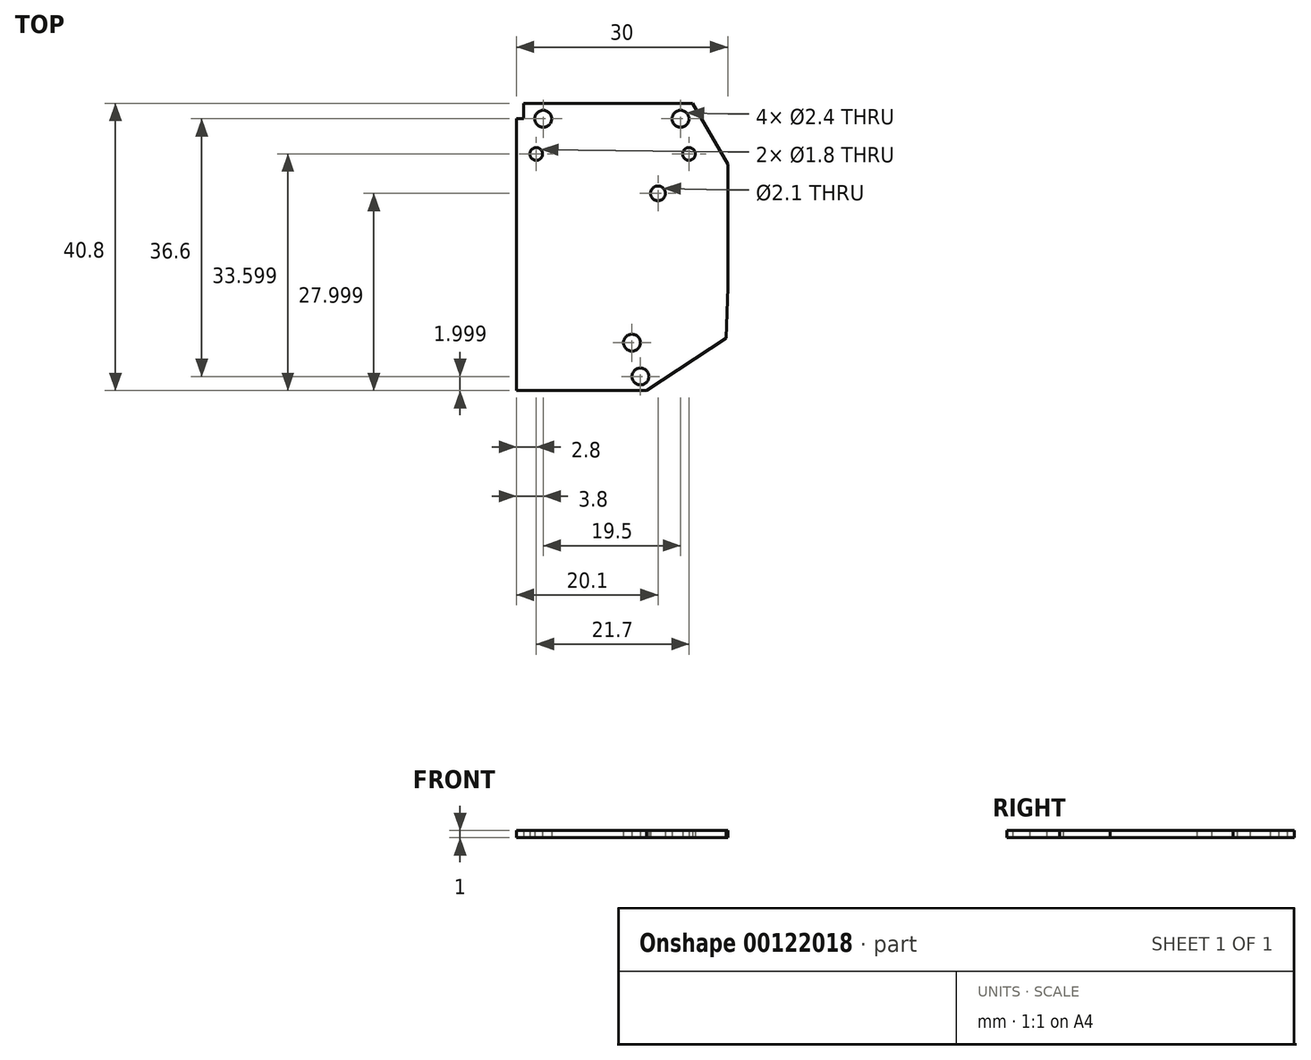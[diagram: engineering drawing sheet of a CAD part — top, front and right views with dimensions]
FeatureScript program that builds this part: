
annotation { "Feature Type Name" : "Feature", "Feature Type Description" : "" }
export const myFeature = defineFeature(function(context is Context, id is Id, definition is map)
    precondition{}
    {
        {
            var Q0;
            Q0=qCreatedBy(makeId("Top.planeOp"),FACE);
            var sketch = newSketch(context, id + "F0", { "sketchPlane" : qUnion([Q0])});
            skLineSegment(sketch, "E0.bottom", {"start": v(-1.47, 15.69) * mm, "end": v(27.53, 15.69) * mm, "construction": true});
            skLineSegment(sketch, "E0.top", {"start": v(-1.47, -22.31) * mm, "end": v(27.53, -22.31) * mm, "construction": true});
            skLineSegment(sketch, "E0.left", {"start": v(-1.47, 15.69) * mm, "end": v(-1.47, -22.31) * mm, "construction": true});
            skLineSegment(sketch, "E0.right", {"start": v(27.53, 15.69) * mm, "end": v(27.53, -22.31) * mm});
            skLineSegment(sketch, "E1.0", {"start": v(-1.47, 13.29) * mm, "end": v(27.53, 13.29) * mm, "construction": true});
            skPoint(sketch, "E2", {"position": v(1.33, 13.29) * mm});
            skPoint(sketch, "E3", {"position": v(20.83, 13.29) * mm});
            skCircle(sketch, "E4", {"center": v(1.33, 13.29) * mm, "radius": 1.2 * mm});
            skCircle(sketch, "E5", {"center": v(20.83, 13.29) * mm, "radius": 1.2 * mm});
            skLineSegment(sketch, "E6.0", {"start": v(-1.47, 2.69) * mm, "end": v(27.53, 2.69) * mm, "construction": true});
            skPoint(sketch, "E7", {"position": v(20.83, 2.69) * mm});
            skPoint(sketch, "E8", {"position": v(17.63, 2.69) * mm});
            skCircle(sketch, "E9", {"center": v(17.63, 2.69) * mm, "radius": 1.05 * mm});
            skLineSegment(sketch, "E10.0", {"start": v(-1.47, -18.51) * mm, "end": v(27.53, -18.51) * mm, "construction": true});
            skPoint(sketch, "E11", {"position": v(17.63, -18.51) * mm});
            skPoint(sketch, "E12", {"position": v(13.93, -18.51) * mm});
            skCircle(sketch, "E13", {"center": v(13.93, -18.51) * mm, "radius": 1.2 * mm});
            skLineSegment(sketch, "E14.0", {"start": v(-1.47, 8.29) * mm, "end": v(27.53, 8.29) * mm, "construction": true});
            skPoint(sketch, "E15", {"position": v(20.83, 8.29) * mm});
            skPoint(sketch, "E16", {"position": v(1.33, 8.29) * mm});
            skPoint(sketch, "E17", {"position": v(22.03, 8.29) * mm});
            skPoint(sketch, "E18", {"position": v(0.33, 8.29) * mm});
            skCircle(sketch, "E19", {"center": v(0.33, 8.29) * mm, "radius": 0.9 * mm});
            skCircle(sketch, "E20", {"center": v(22.03, 8.29) * mm, "radius": 0.9 * mm});
            skLineSegment(sketch, "E21.0", {"start": v(-2.47, 15.69) * mm, "end": v(-2.47, -22.31) * mm});
            skLineSegment(sketch, "E22.0", {"start": v(-1.47, 15.49) * mm, "end": v(27.53, 15.49) * mm});
            skLineSegment(sketch, "E23", {"start": v(-1.47, 13.29) * mm, "end": v(-2.47, 13.29) * mm});
            skLineSegment(sketch, "E24.0", {"start": v(-1.47, -25.31) * mm, "end": v(27.53, -25.31) * mm});
            skLineSegment(sketch, "E25", {"start": v(-1.47, -25.31) * mm, "end": v(-1.47, -22.31) * mm});
            skLineSegment(sketch, "E26", {"start": v(27.53, -25.31) * mm, "end": v(27.53, -22.31) * mm, "construction": true});
            skPoint(sketch, "E27", {"position": v(13.53, -25.31) * mm});
            skPoint(sketch, "E28", {"position": v(16.03, -25.31) * mm});
            skPoint(sketch, "E29", {"position": v(27.53, -17.71) * mm});
            skLineSegment(sketch, "E30", {"start": v(27.53, -17.71) * mm, "end": v(16.03, -25.31) * mm});
            skLineSegment(sketch, "E31", {"start": v(-2.47, -22.31) * mm, "end": v(-2.47, -25.31) * mm});
            skLineSegment(sketch, "E32", {"start": v(-2.47, -25.31) * mm, "end": v(-1.47, -25.31) * mm});
            skLineSegment(sketch, "E33", {"start": v(-1.47, 15.49) * mm, "end": v(-1.47, 13.29) * mm});
            skPoint(sketch, "E34", {"position": v(13.93, -22.31) * mm});
            skLineSegment(sketch, "E35.0", {"start": v(-1.47, -23.31) * mm, "end": v(27.53, -23.31) * mm, "construction": true});
            skPoint(sketch, "E36", {"position": v(15.13, -23.31) * mm});
            skPoint(sketch, "E37", {"position": v(27.53, -23.31) * mm});
            skCircle(sketch, "E38", {"center": v(15.13, -23.31) * mm, "radius": 1.2 * mm});
            skSolve(sketch);
        }
        {
            var Q0;
            Q0=makeQuery(id+"F0.imprint","IMPRINT",FACE,{"disambiguationData":[TD([[makeQuery(id+"F0.imprint","IMPRINT",EDGE,{"derivedFrom":sQuery(id+"F0.wireOp",EDGE,"E4")}),-1.0]])]});
            extrude(context, id + "F1", {"entities" : qUnion([Q0]), "depth" : 1 * mm});
        }
        {
            var Q0;
            Q0=makeQuery(id+"F1.opExtrude","SWEPT_EDGE",EDGE,{"disambiguationData":[OSD([sQuery(id+"F0.wireOp",EDGE,"E0.top"),sQuery(id+"F0.wireOp",EDGE,"E0.right")])]});
            chamfer(context, id + "F2", {"entities" : qUnion([Q0]), "chamferType" : ChamferType.OFFSET_ANGLE, "width" : 5 * mm, "oppositeDirection" : false, "angle" : 60 * degree, "tangentPropagation" : true});
        }
    });
